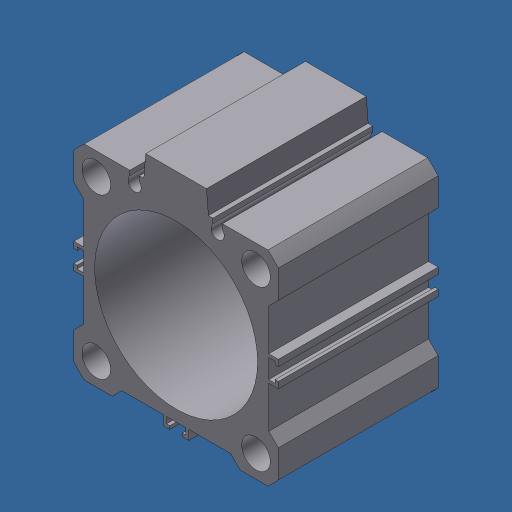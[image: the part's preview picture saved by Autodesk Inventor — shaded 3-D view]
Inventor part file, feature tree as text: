
AUTODESK INVENTOR PART (.ipt)
format: ipt  version: 2024.3 (Build 283343000, 343)  size: 230,912 bytes
history: native  units: mm (DEFAULTED — no unit token found)
features: other x1, extrude x1, hole x1
ambient origin geometry x8: Origin, YZ Plane, XZ Plane, XY Plane, X Axis, Y Axis, Z Axis, Center Point
bodies: Body1 (feature_tree)
feature tree (3):
  other  "Finish - None"
  extrude  "SMC, 50MM"  Depth=86.0mm
  hole  "Hole1"  [1 undecoded]
note: 1 required parameter value undecoded (feature->parameter linkage not recoverable at this tier; creation-order binding heuristic only, values carry confidence <= 0.55)
